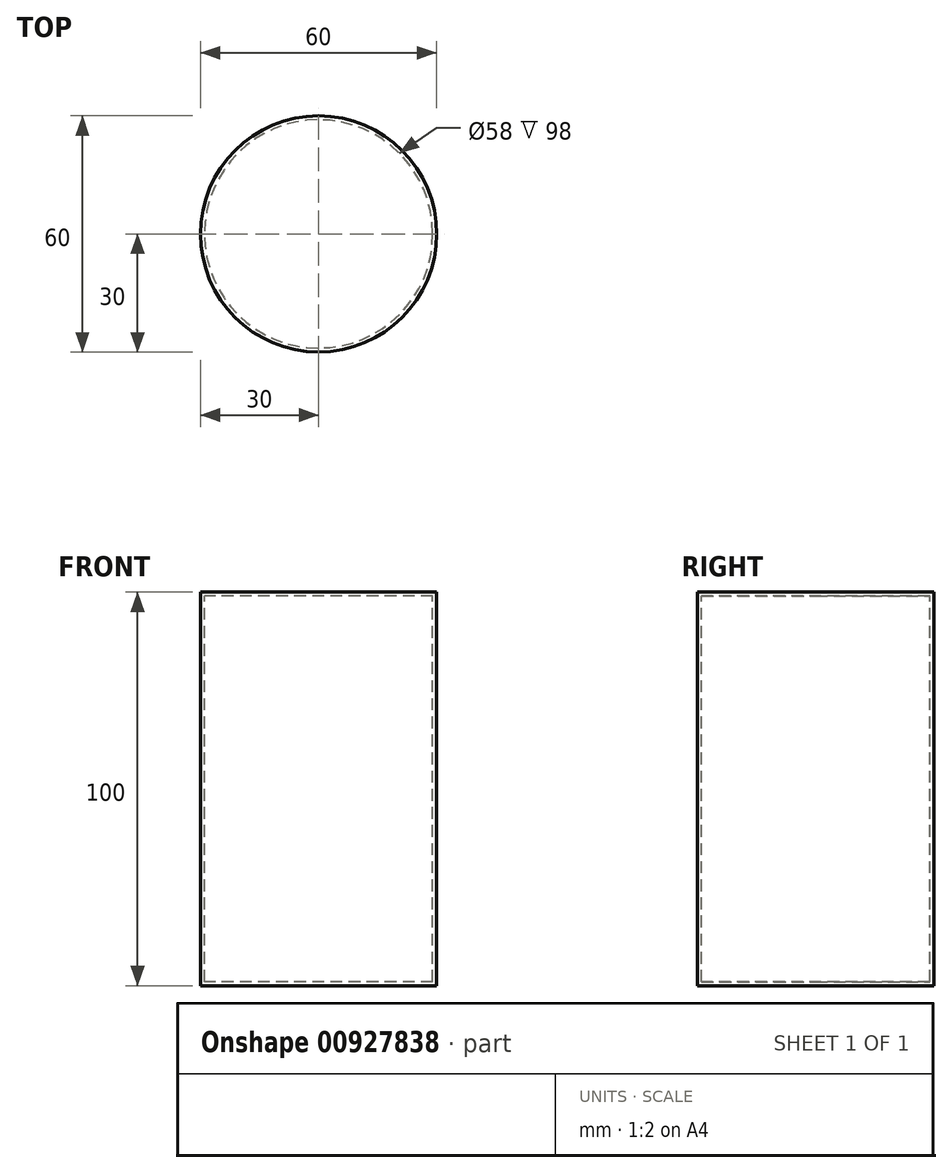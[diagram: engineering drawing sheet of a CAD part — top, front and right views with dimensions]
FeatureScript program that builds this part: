
annotation { "Feature Type Name" : "Feature", "Feature Type Description" : "" }
export const myFeature = defineFeature(function(context is Context, id is Id, definition is map)
    precondition{}
    {
        {
            var Q0;
            Q0=qCreatedBy(makeId("Front.planeOp"),FACE);
            var sketch = newSketch(context, id + "F0", { "sketchPlane" : qUnion([Q0])});
            skLineSegment(sketch, "E0", {"start": v(0, 9.72) * mm, "end": v(0, -7.68) * mm, "construction": true});
            skLineSegment(sketch, "E1.bottom", {"start": v(29, 49) * mm, "end": v(0, 49) * mm});
            skLineSegment(sketch, "E1.top", {"start": v(29, -49) * mm, "end": v(0, -49) * mm});
            skLineSegment(sketch, "E1.left", {"start": v(29, 49) * mm, "end": v(29, -49) * mm});
            skLineSegment(sketch, "E1.right", {"start": v(0, 9.72) * mm, "end": v(0, -7.68) * mm});
            skPoint(sketch, "E1.middle", {"position": v(14.5, 0) * mm});
            skLineSegment(sketch, "E2.bottom", {"start": v(0, 50) * mm, "end": v(30, 50) * mm});
            skLineSegment(sketch, "E2.top", {"start": v(0, -50) * mm, "end": v(30, -50) * mm});
            skLineSegment(sketch, "E2.left", {"start": v(0, 50) * mm, "end": v(0, 49) * mm});
            skLineSegment(sketch, "E2.right", {"start": v(30, 50) * mm, "end": v(30, -50) * mm});
            skLineSegment(sketch, "E3.trimOffspring", {"start": v(0, -49) * mm, "end": v(0, -50) * mm});
            skSolve(sketch);
        }
        {
            var Q0;
            Q0 = qSketchRegion(id + "F0", true);
            var Q1;
            Q1=sQuery(id+"F0.wireOp",EDGE,"E1.right");
            revolve(context, id + "F1", {"surfaceOperationType" : NewSurfaceOperationType.NEW, "entities" : qUnion([Q0]), "axis" : qUnion([Q1]), "revolveType" : RevolveType.FULL});
        }
    });
